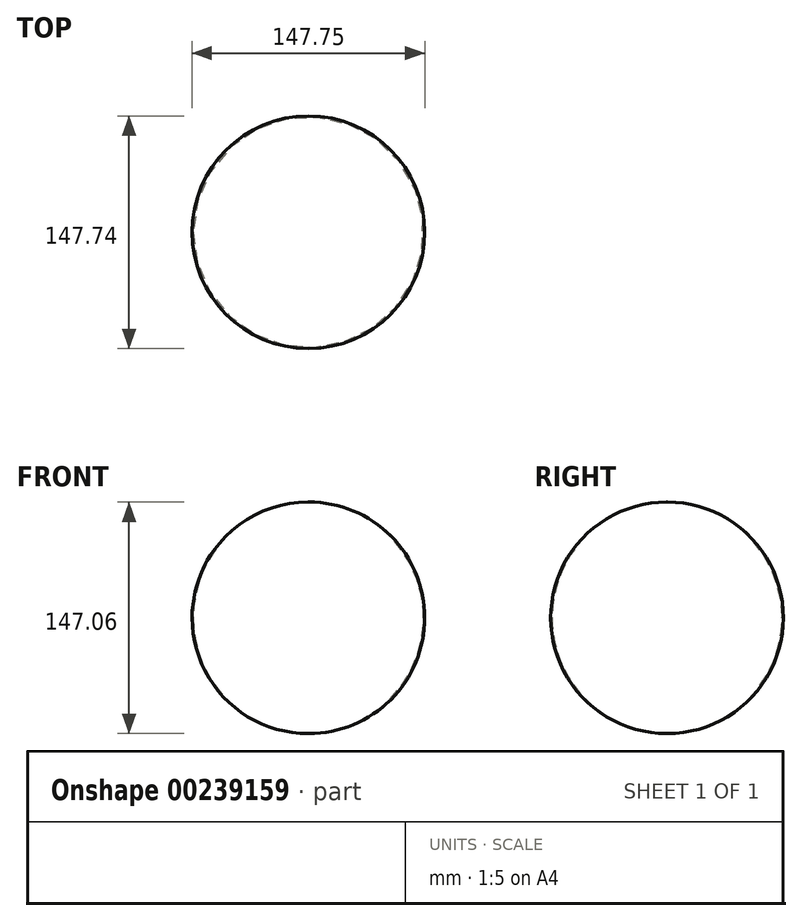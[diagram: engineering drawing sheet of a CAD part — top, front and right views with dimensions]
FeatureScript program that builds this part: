
annotation { "Feature Type Name" : "Feature", "Feature Type Description" : "" }
export const myFeature = defineFeature(function(context is Context, id is Id, definition is map)
    precondition{}
    {
        {
            var Q0;
            Q0=qCreatedBy(makeId("Front.planeOp"),FACE);
            var sketch = newSketch(context, id + "F0", { "sketchPlane" : qUnion([Q0])});
            skArc(sketch, "E0", {"start": v(0.34, -73.53) * mm, "mid": v(73.53, 0) * mm, "end": v(0.34, 73.53) * mm});
            skLineSegment(sketch, "E1", {"start": v(0.34, 73.53) * mm, "end": v(0.34, -73.53) * mm});
            skSolve(sketch);
        }
        {
            var Q0;
            Q0=makeQuery(id+"F0.imprint","IMPRINT",FACE,{"disambiguationData":[TD([[makeQuery(id+"F0.imprint","IMPRINT",EDGE,{"derivedFrom":sQuery(id+"F0.wireOp",EDGE,"E0")}),1.0]])]});
            var Q1;
            Q1=sQuery(id+"F0.wireOp",EDGE,"E1");
            revolve(context, id + "F1", {"entities" : qUnion([Q0]), "axis" : qUnion([Q1]), "revolveType" : RevolveType.FULL});
        }
    });
